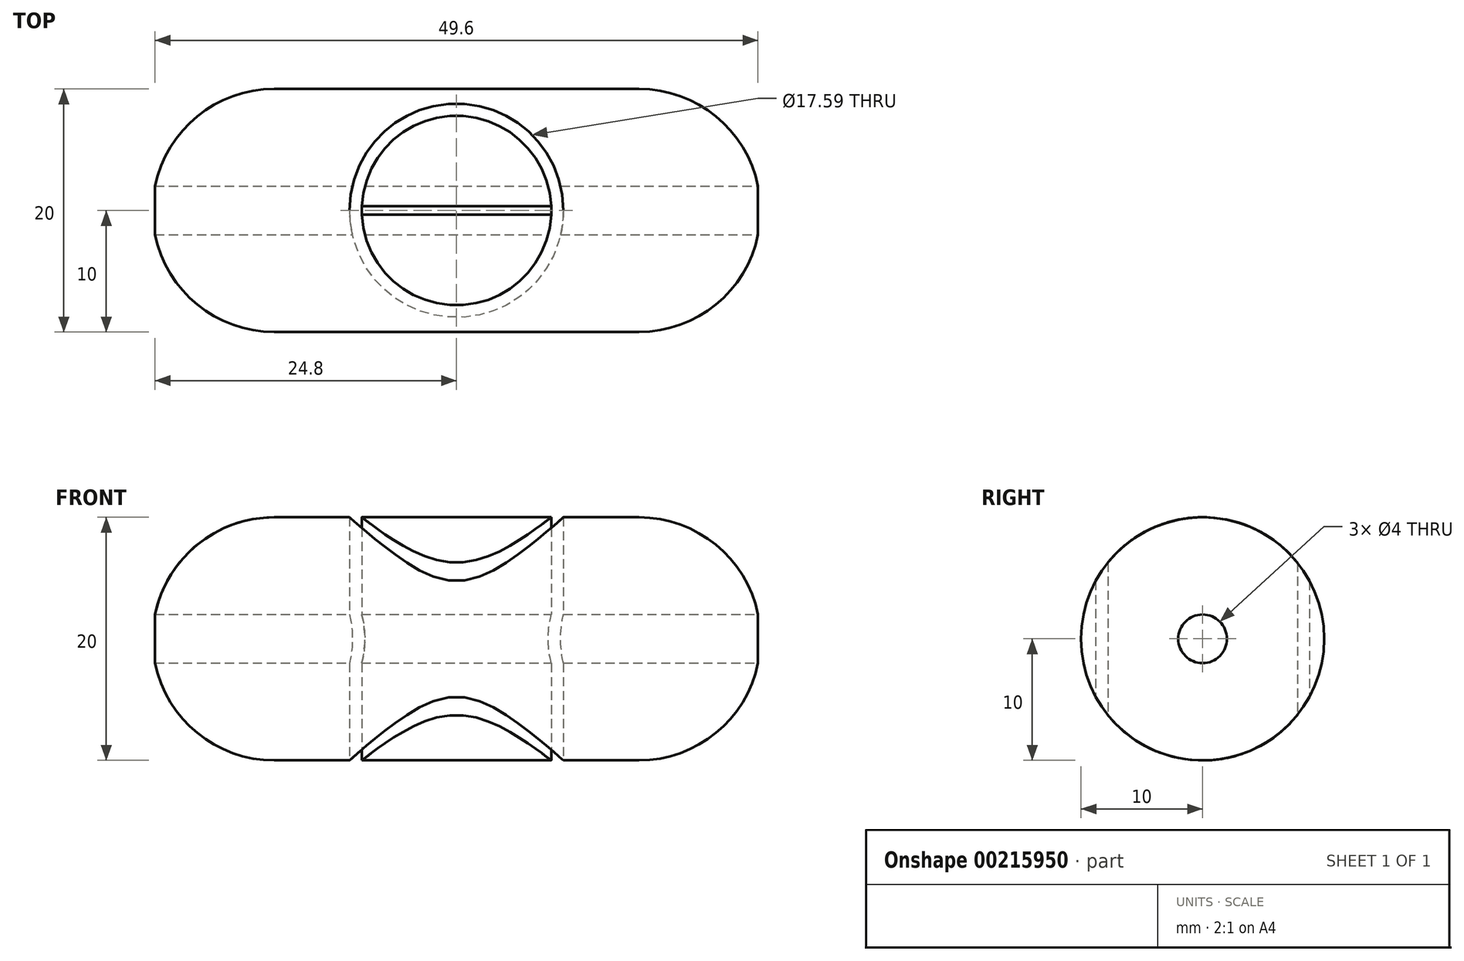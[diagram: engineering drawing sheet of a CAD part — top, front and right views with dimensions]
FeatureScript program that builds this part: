
annotation { "Feature Type Name" : "Feature", "Feature Type Description" : "" }
export const myFeature = defineFeature(function(context is Context, id is Id, definition is map)
    precondition{}
    {
        {
            var Q0;
            Q0=qCreatedBy(makeId("Top.planeOp"),FACE);
            var sketch = newSketch(context, id + "F0", { "sketchPlane" : qUnion([Q0])});
            skLineSegment(sketch, "E0.bottom", {"start": v(25, -10) * mm, "end": v(-25, -10) * mm});
            skLineSegment(sketch, "E0.top", {"start": v(25, 10) * mm, "end": v(-25, 10) * mm});
            skLineSegment(sketch, "E0.left", {"start": v(25, -10) * mm, "end": v(25, 10) * mm});
            skLineSegment(sketch, "E0.right", {"start": v(-25, -10) * mm, "end": v(-25, 10) * mm});
            skPoint(sketch, "E0.middle", {"position": v(0, 0) * mm});
            skCircle(sketch, "E1", {"center": v(0, 0) * mm, "radius": 8.8 * mm});
            skCircle(sketch, "E2.0", {"center": v(0, 0) * mm, "radius": 7.8 * mm});
            skSolve(sketch);
        }
        {
            var Q0;
            Q0=makeQuery(id+"F0.imprint","IMPRINT",FACE,{"disambiguationData":[TD([[makeQuery(id+"F0.imprint","IMPRINT",EDGE,{"derivedFrom":sQuery(id+"F0.wireOp",EDGE,"E0.bottom")}),-1.0]])]});
            var Q1;
            Q1=makeQuery(id+"F0.imprint","IMPRINT",FACE,{"disambiguationData":[TD([[makeQuery(id+"F0.imprint","IMPRINT",EDGE,{"derivedFrom":sQuery(id+"F0.wireOp",EDGE,"E2.0")}),1.0]])]});
            extrude(context, id + "F1", {"entities" : qUnion([Q0, Q1]), "depth" : 10 * mm, "hasSecondDirection" : true, "secondDirectionOppositeDirection" : true, "secondDirectionDepth" : 10 * mm});
        }
        {
            var Q0;
            Q0=makeQuery(id+"F1.opExtrude","CAP_EDGE",EDGE,{"disambiguationData":[OSD([sQuery(id+"F0.wireOp",EDGE,"E0.bottom")])],"isStart":false});
            var Q1;
            Q1=makeQuery(id+"F1.opExtrude","CAP_EDGE",EDGE,{"disambiguationData":[OSD([sQuery(id+"F0.wireOp",EDGE,"E0.top")])],"isStart":false});
            var Q2;
            Q2=makeQuery(id+"F1.opExtrude","CAP_EDGE",EDGE,{"disambiguationData":[OSD([sQuery(id+"F0.wireOp",EDGE,"E0.bottom")])],"isStart":true});
            var Q3;
            Q3=makeQuery(id+"F1.opExtrude","CAP_EDGE",EDGE,{"disambiguationData":[OSD([sQuery(id+"F0.wireOp",EDGE,"E0.top")])],"isStart":true});
            var Q4;
            Q4=makeQuery(id+"F1.opExtrude","SWEPT_EDGE",EDGE,{"disambiguationData":[OSD([sQuery(id+"F0.wireOp",EDGE,"E0.top"),sQuery(id+"F0.wireOp",EDGE,"E0.right")])]});
            var Q5;
            Q5=makeQuery(id+"F1.opExtrude","CAP_EDGE",EDGE,{"disambiguationData":[OSD([sQuery(id+"F0.wireOp",EDGE,"E0.right")])],"isStart":false});
            var Q6;
            Q6=makeQuery(id+"F1.opExtrude","CAP_EDGE",EDGE,{"disambiguationData":[OSD([sQuery(id+"F0.wireOp",EDGE,"E0.right")])],"isStart":true});
            var Q7;
            Q7=makeQuery(id+"F1.opExtrude","SWEPT_EDGE",EDGE,{"disambiguationData":[OSD([sQuery(id+"F0.wireOp",EDGE,"E0.bottom"),sQuery(id+"F0.wireOp",EDGE,"E0.right")])]});
            var Q8;
            Q8=makeQuery(id+"F1.opExtrude","SWEPT_EDGE",EDGE,{"disambiguationData":[OSD([sQuery(id+"F0.wireOp",EDGE,"E0.top"),sQuery(id+"F0.wireOp",EDGE,"E0.left")])]});
            var Q9;
            Q9=makeQuery(id+"F1.opExtrude","CAP_EDGE",EDGE,{"disambiguationData":[OSD([sQuery(id+"F0.wireOp",EDGE,"E0.left")])],"isStart":false});
            var Q10;
            Q10=makeQuery(id+"F1.opExtrude","SWEPT_EDGE",EDGE,{"disambiguationData":[OSD([sQuery(id+"F0.wireOp",EDGE,"E0.bottom"),sQuery(id+"F0.wireOp",EDGE,"E0.left")])]});
            var Q11;
            Q11=makeQuery(id+"F1.opExtrude","CAP_EDGE",EDGE,{"disambiguationData":[OSD([sQuery(id+"F0.wireOp",EDGE,"E0.left")])],"isStart":true});
            fillet(context, id + "F2", {"entities" : qUnion([Q0, Q1, Q2, Q3, Q4, Q5, Q6, Q7, Q8, Q9, Q10, Q11]), "radius" : 10 * mm, "tangentPropagation" : true, "allowEdgeOverflow" : false});
        }
        {
            var Q0;
            Q0=qCreatedBy(makeId("Right.planeOp"),FACE);
            var sketch = newSketch(context, id + "F3", { "sketchPlane" : qUnion([Q0])});
            skCircle(sketch, "E3", {"center": v(0, 0) * mm, "radius": 2 * mm});
            skSolve(sketch);
        }
        {
            var Q0;
            Q0=makeQuery(id+"F3.imprint","IMPRINT",FACE,{"disambiguationData":[TD([[makeQuery(id+"F3.imprint","IMPRINT",EDGE,{"derivedFrom":sQuery(id+"F3.wireOp",EDGE,"E3")}),1.0]])]});
            extrude(context, id + "F4", {"entities" : qUnion([Q0]), "operationType" : NewBodyOperationType.REMOVE, "oppositeDirection" : true, "depth" : 25 * mm, "hasSecondDirection" : true, "secondDirectionOppositeDirection" : false, "secondDirectionDepth" : 25 * mm});
        }
        {
            var Q0;
            Q0=qCreatedBy(makeId("Right.planeOp"),FACE);
            var sketch = newSketch(context, id + "F5", { "sketchPlane" : qUnion([Q0])});
            skCircle(sketch, "E4", {"center": v(0, 0) * mm, "radius": 10 * mm});
            skCircle(sketch, "E5.0", {"center": v(0, 0) * mm, "radius": 15 * mm});
            skSolve(sketch);
        }
        {
            var Q0;
            Q0=makeQuery(id+"F5.imprint","IMPRINT",FACE,{"disambiguationData":[TD([[makeQuery(id+"F5.imprint","IMPRINT",EDGE,{"derivedFrom":sQuery(id+"F5.wireOp",EDGE,"E4")}),-1.0]])]});
            extrude(context, id + "F6", {"entities" : qUnion([Q0]), "operationType" : NewBodyOperationType.REMOVE, "oppositeDirection" : true, "depth" : 25 * mm, "hasSecondDirection" : true, "secondDirectionOppositeDirection" : false, "secondDirectionDepth" : 25 * mm});
        }
    });
